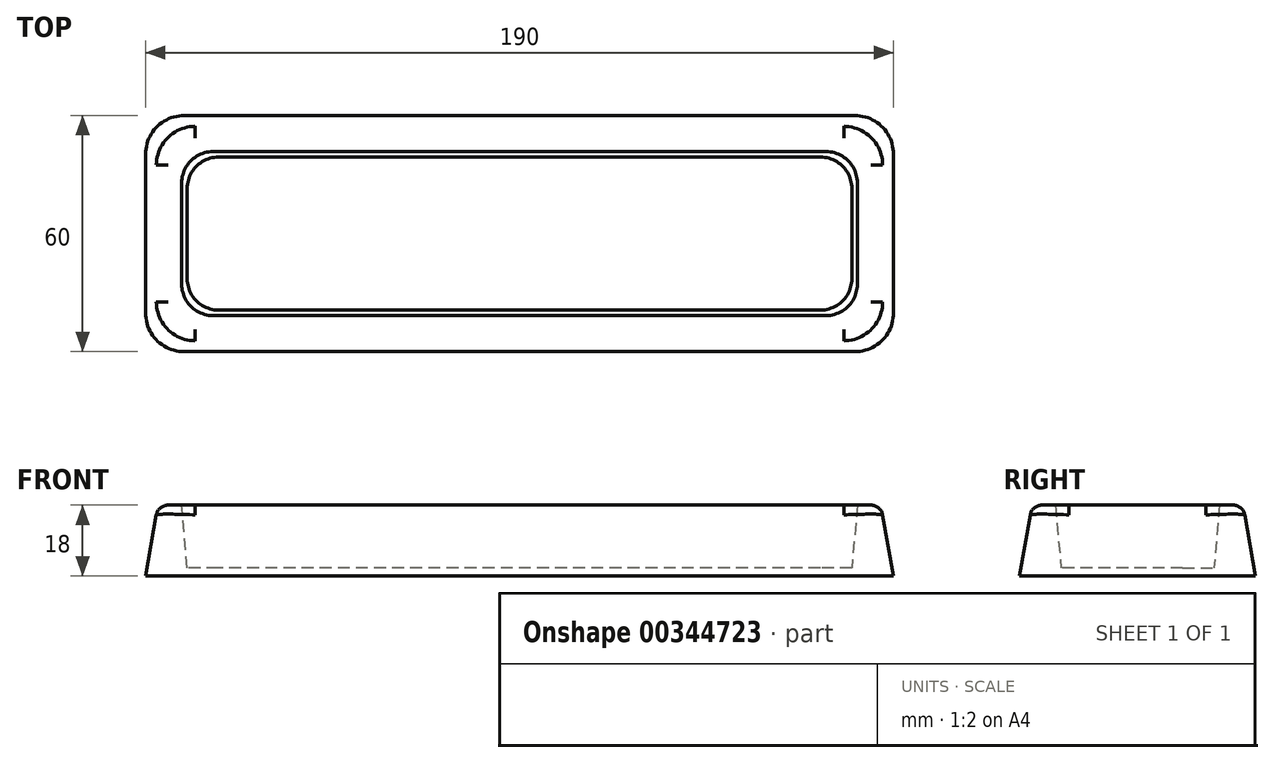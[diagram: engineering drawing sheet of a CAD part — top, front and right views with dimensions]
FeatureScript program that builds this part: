
annotation { "Feature Type Name" : "Feature", "Feature Type Description" : "" }
export const myFeature = defineFeature(function(context is Context, id is Id, definition is map)
    precondition{}
    {
        {
            var Q0;
            Q0=qCreatedBy(makeId("Top.planeOp"),FACE);
            var sketch = newSketch(context, id + "F0", { "sketchPlane" : qUnion([Q0])});
            skLineSegment(sketch, "E0.bottom", {"start": v(0, 0) * mm, "end": v(190, 0) * mm});
            skLineSegment(sketch, "E0.top", {"start": v(0, 60) * mm, "end": v(190, 60) * mm});
            skLineSegment(sketch, "E0.left", {"start": v(0, 0) * mm, "end": v(0, 60) * mm});
            skLineSegment(sketch, "E0.right", {"start": v(190, 0) * mm, "end": v(190, 60) * mm});
            skSolve(sketch);
        }
        {
            var Q0;
            Q0=makeQuery(id+"F0.imprint","IMPRINT",FACE,{"disambiguationData":[TD([[makeQuery(id+"F0.imprint","IMPRINT",EDGE,{"derivedFrom":sQuery(id+"F0.wireOp",EDGE,"E0.bottom")}),1.0]])]});
            extrude(context, id + "F1", {"entities" : qUnion([Q0]), "depth" : 18 * mm, "hasDraft" : true, "draftAngle" : 10 * degree, "draftPullDirection" : true});
        }
        {
            var Q0;
            Q0=makeQuery(id+"F1.opExtrude","CAP_FACE",FACE,{"disambiguationData":[OSD([sQuery(id+"F0.wireOp",EDGE,"E0.bottom"),sQuery(id+"F0.wireOp",EDGE,"E0.top"),sQuery(id+"F0.wireOp",EDGE,"E0.left"),sQuery(id+"F0.wireOp",EDGE,"E0.right")])],"isStart":false});
            var sketch = newSketch(context, id + "F2", { "sketchPlane" : qUnion([Q0])});
            skLineSegment(sketch, "E1.bottom", {"start": v(9.17, 50.83) * mm, "end": v(180.83, 50.83) * mm});
            skLineSegment(sketch, "E1.top", {"start": v(9.17, 9.17) * mm, "end": v(180.83, 9.17) * mm});
            skLineSegment(sketch, "E1.left", {"start": v(9.17, 50.83) * mm, "end": v(9.17, 9.17) * mm});
            skLineSegment(sketch, "E1.right", {"start": v(180.83, 50.83) * mm, "end": v(180.83, 9.17) * mm});
            skSolve(sketch);
        }
        {
            var Q0;
            Q0=makeQuery(id+"F2.imprint","IMPRINT",FACE,{"disambiguationData":[TD([[makeQuery(id+"F2.imprint","IMPRINT",EDGE,{"derivedFrom":sQuery(id+"F2.wireOp",EDGE,"E1.bottom")}),-1.0]])]});
            extrude(context, id + "F3", {"entities" : qUnion([Q0]), "operationType" : NewBodyOperationType.ADD, "oppositeDirection" : true, "depth" : 16 * mm, "hasDraft" : true, "draftAngle" : 5 * degree, "draftPullDirection" : true});
        }
        {
            var Q0;
            Q0=makeQuery(id+"F1.opExtrude","CAP_FACE",FACE,{"disambiguationData":[OSD([sQuery(id+"F0.wireOp",EDGE,"E0.bottom"),sQuery(id+"F0.wireOp",EDGE,"E0.top"),sQuery(id+"F0.wireOp",EDGE,"E0.left"),sQuery(id+"F0.wireOp",EDGE,"E0.right")])],"isStart":false});
            var sketch = newSketch(context, id + "F4", { "sketchPlane" : qUnion([Q0])});
            skLineSegment(sketch, "E2.bottom", {"start": v(9.17, 50.83) * mm, "end": v(180.83, 50.83) * mm});
            skLineSegment(sketch, "E2.top", {"start": v(9.17, 9.17) * mm, "end": v(180.83, 9.17) * mm});
            skLineSegment(sketch, "E2.left", {"start": v(9.17, 50.83) * mm, "end": v(9.17, 9.17) * mm});
            skLineSegment(sketch, "E2.right", {"start": v(180.83, 50.83) * mm, "end": v(180.83, 9.17) * mm});
            skSolve(sketch);
        }
        {
            var Q0;
            Q0=makeQuery(id+"F4.imprint","IMPRINT",FACE,{"disambiguationData":[TD([[makeQuery(id+"F4.imprint","IMPRINT",EDGE,{"derivedFrom":sQuery(id+"F4.wireOp",EDGE,"E2.bottom")}),-1.0]])]});
            extrude(context, id + "F5", {"entities" : qUnion([Q0]), "operationType" : NewBodyOperationType.REMOVE, "oppositeDirection" : true, "depth" : 16 * mm, "hasDraft" : true, "draftAngle" : 5 * degree, "draftPullDirection" : true});
        }
        {
            var Q0;
            Q0=makeQuery(id+"F5.boolean.opBoolean","COPY",EDGE,{"derivedFrom":makeQuery(id+"F5.opExtrude","SWEPT_EDGE",EDGE,{"disambiguationData":[OSD([sQuery(id+"F4.wireOp",EDGE,"E2.bottom"),sQuery(id+"F4.wireOp",EDGE,"E2.left")])]})});
            var Q1;
            Q1=makeQuery(id+"F5.boolean.opBoolean","COPY",EDGE,{"derivedFrom":makeQuery(id+"F5.opExtrude","SWEPT_EDGE",EDGE,{"disambiguationData":[OSD([sQuery(id+"F4.wireOp",EDGE,"E2.top"),sQuery(id+"F4.wireOp",EDGE,"E2.left")])]})});
            var Q2;
            Q2=makeQuery(id+"F5.boolean.opBoolean","COPY",EDGE,{"derivedFrom":makeQuery(id+"F5.opExtrude","SWEPT_EDGE",EDGE,{"disambiguationData":[OSD([sQuery(id+"F4.wireOp",EDGE,"E2.top"),sQuery(id+"F4.wireOp",EDGE,"E2.right")])]})});
            var Q3;
            Q3=makeQuery(id+"F5.boolean.opBoolean","COPY",EDGE,{"derivedFrom":makeQuery(id+"F5.opExtrude","SWEPT_EDGE",EDGE,{"disambiguationData":[OSD([sQuery(id+"F4.wireOp",EDGE,"E2.bottom"),sQuery(id+"F4.wireOp",EDGE,"E2.right")])]})});
            fillet(context, id + "F6", {"entities" : qUnion([Q0, Q1, Q2, Q3]), "radius" : 8 * mm, "tangentPropagation" : true, "allowEdgeOverflow" : false});
        }
        {
            var Q0;
            Q0=makeQuery(id+"F1.opExtrude","SWEPT_EDGE",EDGE,{"disambiguationData":[OSD([sQuery(id+"F0.wireOp",EDGE,"E0.top"),sQuery(id+"F0.wireOp",EDGE,"E0.left")])]});
            var Q1;
            Q1=makeQuery(id+"F1.opExtrude","SWEPT_EDGE",EDGE,{"disambiguationData":[OSD([sQuery(id+"F0.wireOp",EDGE,"E0.bottom"),sQuery(id+"F0.wireOp",EDGE,"E0.left")])]});
            var Q2;
            Q2=makeQuery(id+"F1.opExtrude","SWEPT_EDGE",EDGE,{"disambiguationData":[OSD([sQuery(id+"F0.wireOp",EDGE,"E0.bottom"),sQuery(id+"F0.wireOp",EDGE,"E0.right")])]});
            var Q3;
            Q3=makeQuery(id+"F1.opExtrude","SWEPT_EDGE",EDGE,{"disambiguationData":[OSD([sQuery(id+"F0.wireOp",EDGE,"E0.top"),sQuery(id+"F0.wireOp",EDGE,"E0.right")])]});
            fillet(context, id + "F7", {"entities" : qUnion([Q0, Q1, Q2, Q3]), "radius" : 10 * mm, "tangentPropagation" : true, "allowEdgeOverflow" : false});
        }
        {
            var Q0;
            Q0=makeQuery(id+"F5.boolean.opBoolean","COPY",EDGE,{"derivedFrom":makeQuery(id+"F5.opExtrude","CAP_EDGE",EDGE,{"disambiguationData":[OSD([sQuery(id+"F4.wireOp",EDGE,"E2.top")])],"isStart":true})});
            var Q1;
            Q1=makeQuery(id+"F1.opExtrude","CAP_EDGE",EDGE,{"disambiguationData":[OSD([sQuery(id+"F0.wireOp",EDGE,"E0.bottom")])],"isStart":false});
            fillet(context, id + "F8", {"entities" : qUnion([Q0, Q1]), "radius" : 3 * mm, "tangentPropagation" : true, "allowEdgeOverflow" : false});
        }
    });
